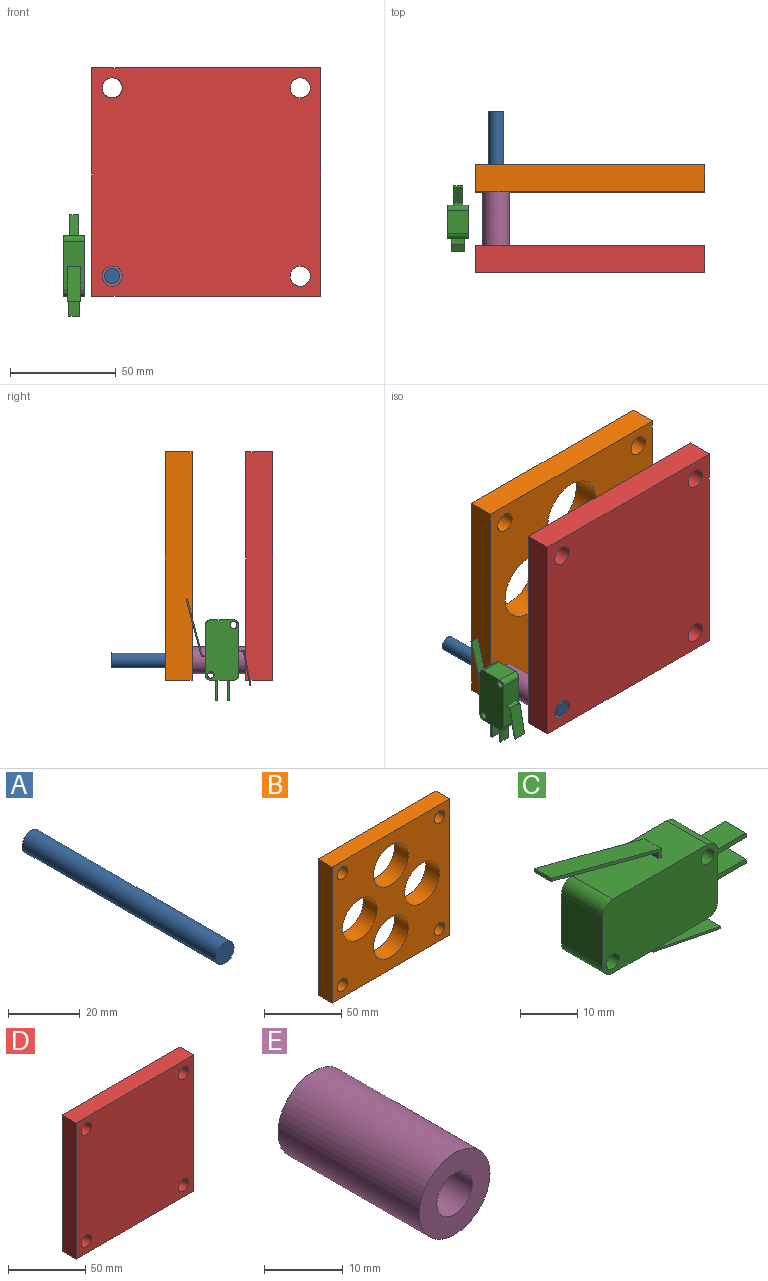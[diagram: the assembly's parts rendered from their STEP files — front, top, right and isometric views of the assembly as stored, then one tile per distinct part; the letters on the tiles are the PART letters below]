
ASSEMBLY  parts=5 mates=7
PART A: 3 faces, bbox 7.1x76.2x7.1 mm
  f0: cylinder r=3.56mm len=76.2mm, axis (0,1,0), area 1702.5mm2, adj f1,f2
  f1: plane 7.11x7.11mm, normal (0,-1,0), area 39.7mm2, adj f0
  f2: plane 7.11x7.11mm, normal (0,1,0), area 39.7mm2, adj f0
PART B: 14 faces, bbox 108x12.7x108 mm
  f0: plane 107.95x12.7mm, normal (0,0,-1), area 1371mm2, adj f1,f3,f12,f13
  f1: plane 107.95x12.7mm, normal (1,0,0), area 1371mm2, adj f0,f2,f12,f13
  f2: plane 107.95x12.7mm, normal (0,0,1), area 1371mm2, adj f1,f3,f12,f13
  f3: plane 107.95x12.7mm, normal (-1,0,0), area 1371mm2, adj f0,f2,f12,f13
  f4: cylinder r=15.88mm len=31.75mm, axis (0,1,0), area 1266.8mm2, adj f12,f13
  f5: cylinder r=15.88mm len=31.75mm, axis (0,1,0), area 1266.8mm2, adj f12,f13
  f6: cylinder r=15.88mm len=31.75mm, axis (0,1,0), area 1266.8mm2, adj f12,f13
  f7: cylinder r=4.76mm len=12.7mm, axis (0,1,0), area 380mm2, adj f12,f13
  f8: cylinder r=4.76mm len=12.7mm, axis (0,1,0), area 380mm2, adj f12,f13
  f9: cylinder r=4.76mm len=12.7mm, axis (0,1,0), area 380mm2, adj f12,f13
  f10: cylinder r=15.88mm len=31.75mm, axis (0,1,0), area 1266.8mm2, adj f12,f13
  f11: cylinder r=4.76mm len=12.7mm, axis (0,1,0), area 380mm2, adj f12,f13
  f12: plane 107.95x107.95mm, normal (0,-1,0), area 8201.3mm2, adj f0,f1,f2,f3,f4,f5,f6,f7
  f13: plane 107.95x107.95mm, normal (0,1,0), area 8201.3mm2, adj f0,f1,f2,f3,f4,f5,f6,f7
PART C: 36 faces, bbox 47.9x10.2x30.6 mm
  f0: plane 23.5x10.16mm, normal (0,0,1), area 236mm2, adj f4,f5,f6,f9,f30,f31,f34,f35
  f1: plane 10.8x10.16mm, normal (-1,0,0), area 109.7mm2, adj f4,f5,f6,f7
  f2: plane 23.5x10.16mm, normal (0,0,-1), area 235.5mm2, adj f4,f5,f7,f8,f12,f13,f14,f15
  f3: plane 10.8x10.16mm, normal (1,0,0), area 99.6mm2, adj f4,f5,f8,f9,f19,f20,f22,f23
  f4: plane 28.58x15.88mm, normal (0,-1,0), area 432.3mm2, adj f0,f1,f2,f3,f6,f7,f8,f9
  f5: plane 28.58x15.88mm, normal (0,1,0), area 432.3mm2, adj f0,f1,f2,f3,f6,f7,f8,f9
  f6: cylinder r=2.54mm len=10.16mm, axis (0,-1,0), area 40.5mm2, adj f0,f1,f4,f5
  f7: cylinder r=2.54mm len=10.16mm, axis (0,1,0), area 40.5mm2, adj f1,f2,f4,f5
  f8: cylinder r=2.54mm len=10.16mm, axis (0,-1,0), area 40.5mm2, adj f2,f3,f4,f5
  f9: cylinder r=2.54mm len=10.16mm, axis (0,1,0), area 40.5mm2, adj f0,f3,f4,f5
  f10: cylinder r=1.59mm len=10.16mm, axis (0,-1,0), area 101.3mm2, adj f4,f5
  f11: cylinder r=1.59mm len=10.16mm, axis (0,-1,0), area 101.3mm2, adj f4,f5
  f12: plane 6.35x2.45mm, normal (-1,0,0), area 15.6mm2, adj f2,f14,f15,f16
  f13: plane 6.35x2.03mm, normal (1,0,0), area 12.9mm2, adj f2,f14,f15,f18
  f14: plane 16.48x5.68mm, normal (0,-1,0), area 9.5mm2, adj f2,f12,f13,f16,f17,f18
  f15: plane 16.48x5.68mm, normal (0,1,0), area 9.5mm2, adj f2,f12,f13,f16,f17,f18
  f16: plane 16.38x6.35mm, normal (-0.19,0,-0.98), area 106mm2, adj f12,f14,f15,f17
  f17: plane 6.35x0.5mm, normal (0.98,0,-0.19), area 3.2mm2, adj f14,f15,f16,f18
  f18: plane 15.97x6.35mm, normal (0.19,0,0.98), area 103.4mm2, adj f13,f14,f15,f17
  f19: plane 9.49x5.08mm, normal (0,0,1), area 48.2mm2, adj f3,f21,f22,f23
  f20: plane 9.49x5.08mm, normal (0,0,-1), area 48.2mm2, adj f3,f21,f22,f23
  f21: plane 5.08x1mm, normal (1,0,0), area 5.1mm2, adj f19,f20,f22,f23
  f22: plane 9.49x1mm, normal (0,-1,0), area 9.5mm2, adj f3,f19,f20,f21
  f23: plane 9.49x1mm, normal (0,1,0), area 9.5mm2, adj f3,f19,f20,f21
  f24: plane 9.49x5.08mm, normal (0,0,1), area 48.2mm2, adj f3,f26,f27,f28
  f25: plane 9.49x5.08mm, normal (0,0,-1), area 48.2mm2, adj f3,f26,f27,f28
  f26: plane 5.08x1mm, normal (1,0,0), area 5.1mm2, adj f24,f25,f27,f28
  f27: plane 9.49x1mm, normal (0,-1,0), area 9.5mm2, adj f3,f24,f25,f26
  f28: plane 9.49x1mm, normal (0,1,0), area 9.5mm2, adj f3,f24,f25,f26
  f29: plane 26.71x7.07mm, normal (-0.26,0,-0.97), area 115.8mm2, adj f30,f33,f34,f35
  f30: plane 4.19x1.41mm, normal (-1,0,0), area 5.9mm2, adj f0,f29,f34,f35
  f31: plane 4.19x1.9mm, normal (1,0,0), area 7.9mm2, adj f0,f32,f34,f35
  f32: plane 27.18x7.19mm, normal (0.26,0,0.97), area 117.8mm2, adj f31,f33,f34,f35
  f33: plane 4.19x0.61mm, normal (-0.97,0,0.26), area 2.7mm2, adj f29,f32,f34,f35
  f34: plane 27.35x9.09mm, normal (0,-1,0), area 18.7mm2, adj f0,f29,f30,f31,f32,f33
  f35: plane 27.35x9.09mm, normal (0,1,0), area 18.7mm2, adj f0,f29,f30,f31,f32,f33
PART D: 10 faces, bbox 108x12.7x108 mm
  f0: plane 107.95x12.7mm, normal (0,0,-1), area 1371mm2, adj f1,f4,f8,f9
  f1: plane 107.95x12.7mm, normal (1,0,0), area 1371mm2, adj f0,f2,f8,f9
  f2: plane 107.95x12.7mm, normal (0,0,1), area 1371mm2, adj f1,f4,f8,f9
  f3: cylinder r=4.76mm len=12.7mm, axis (0,1,0), area 380mm2, adj f8,f9
  f4: plane 107.95x12.7mm, normal (-1,0,0), area 1371mm2, adj f0,f2,f8,f9
  f5: cylinder r=4.76mm len=12.7mm, axis (0,1,0), area 380mm2, adj f8,f9
  f6: cylinder r=4.76mm len=12.7mm, axis (0,1,0), area 380mm2, adj f8,f9
  f7: cylinder r=4.76mm len=12.7mm, axis (0,1,0), area 380mm2, adj f8,f9
  f8: plane 107.95x107.95mm, normal (0,-1,0), area 11368.2mm2, adj f0,f1,f2,f3,f4,f5,f6,f7
  f9: plane 107.95x107.95mm, normal (0,1,0), area 11368.2mm2, adj f0,f1,f2,f3,f4,f5,f6,f7
PART E: 4 faces, bbox 12.7x25.4x12.7 mm
  f0: cylinder r=6.35mm len=25.4mm, axis (0,1,0), area 1013.4mm2, adj f1,f2
  f1: plane 12.7x12.7mm, normal (0,-1,0), area 94.5mm2, adj f0,f3
  f2: plane 12.7x12.7mm, normal (0,1,0), area 94.5mm2, adj f0,f3
  f3: cylinder r=3.2mm len=25.4mm, axis (0,1,0), area 510.8mm2, adj f1,f2
PLACE A t=(-201.3,-43.11,-114.15)mm
PLACE B t=(-86.29,-68.53,-12.75)mm
PLACE C rot(axis=(-0.58,0.58,0.58),120deg) t=(-148.64,-109.17,-142.16)mm
PLACE D t=(-86.29,-81.21,-12.75)mm fixed
PLACE E t=(-130.74,-93.91,-57.2)mm
MATE planar B.f3 <-> D.f4  axis (-1,0,0) through (-140.26,-74.88,-12.75)mm
MATE cylindrical E.f0 <-> A.f0  axis (0,1,0) through (-130.74,-93.91,-57.2)mm
MATE cylindrical A.f0 <-> D.f3  axis (0,1,0) through (-130.74,-119.31,-57.2)mm
MATE parallel D.f4 <-> C.f4  axis (-1,0,0) through (-140.26,-112.96,-12.75)mm
MATE cylindrical B.f8 <-> A.f0  axis (0,1,0) through (-130.74,-68.53,-57.2)mm
MATE planar E.f0 <-> D.f9  axis (0,-1,0) through (-130.74,-106.61,-57.2)mm
MATE planar D.f8 <-> A.f0  axis (0,-1,0) through (-86.29,-119.31,-12.75)mm
